# Revit family: HeatPump_AirToWater_Rheem_30kW_Vertical_LowGWP
name_source: partatom
category: Mechanical Equipment
units: mm (PartAtom-declared; Revit-internal decimal feet)

## family parameters
Always vertical = Yes
Classification = None
Cut with Voids When Loaded = No
OmniClass Number = 23.33.17.00
OmniClass Title = Heat Pumps
Part Type = Normal
Room Calculation Point = No
Round Connector Dimension = Use Diameter
Shared = No
Work Plane-Based = No

## types (2) — shared parameters
ApparentLoad = 30 VA
Assembly Code = D3020
BodyMaterial = Aluminium_PowderCoat_Rheem_White
FanHeight = 114 mm  [stored 0.374016 ft]
FanMaterial = <By Category>
IfcExportAs = IfcPump
IfcExportType = USERDEFINED
Manufacturer = Rheem
ManufacturerOverallDepth = 807 mm
ManufacturerOverallHeight = 1404 mm  [stored 4.6063 ft]
ManufacturerOverallWidth = 1857 mm
ManufacturerURLProductSpecific = https://www.rheem.com.au
ModifiedIssue = 20240801 $
PowerFactor = 1
ScreenMaterial = Metal_Vent_Rheem_HeatPump_Wire
URL = https://www.rheem.com.au
Uniclass2015Code = Pr_70_60_37_04
Uniclass2015Title = Air to water heat pumps
Uniclass2015Version = v1.33
Voltage = 230 V
zero-valued in all types: Default Elevation

## per-type parameters (varying)
| type | Description | FanFrame | ManufacturerSpecCode | Model | Type Comments |
| Ducted (95203500) | Rheem's Commercial Air to Water (A2W) Heat Pump is designed with the commercial user in mind. A truly commercial grade heat pump that delivers hot water up to 65°C with a system Coefficient of Performance (COP) up to 4.0 at 20°C ambient. Ducted models are designed to be connected to ducting to convey cold discharge air away from the heat pump air inlet if a sufficient supply of heat energy is not available in the installation area. Models are also available in vertical, horizontal and stackable options. | Yes | 95203500 | 95203500 | HeatPump - AirToWater - 35kW - Vertical - Ducted |
| Non Ducted (95303500) | Rheem's Commercial Air to Water (A2W) Heat Pump is designed with the commercial user in mind. A truly commercial grade heat pump that delivers hot water up to 65°C with a system Coefficient of Performance (COP) up to 4.0 at 20°C ambient. Non ducted models are generally designed for outdoor installations. Non ducted models may be installed indoors, without ducting, if a sufficient supply of heat energy is available. Models are also available in vertical, horizontal and stackable options. | No | 95303500 | 95303500 | HeatPump - AirToWater - 35kW - Vertical - Non Ducted |

note: [stored X ft] marks values corroborated as IEEE doubles in the binary element streams (Revit-internal decimal feet)

## geometry (parser evidence)
native form markers: Sweep x7
no freeform markers — native parametric forms only
